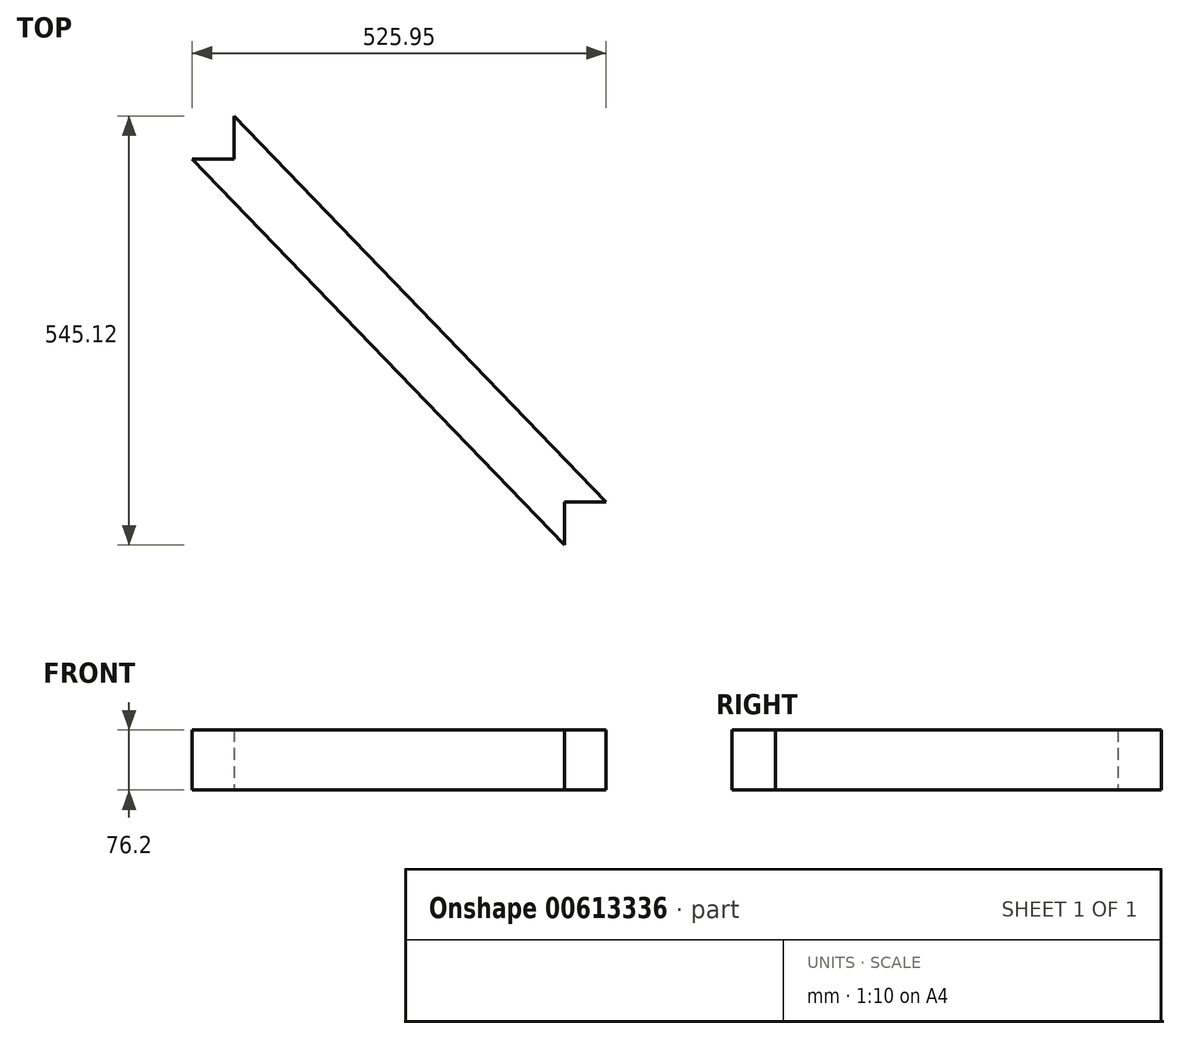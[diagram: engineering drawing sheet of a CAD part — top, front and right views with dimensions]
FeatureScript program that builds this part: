
annotation { "Feature Type Name" : "Feature", "Feature Type Description" : "" }
export const myFeature = defineFeature(function(context is Context, id is Id, definition is map)
    precondition{}
    {
        {
            var Q0;
            Q0=qCreatedBy(makeId("Top.planeOp"),FACE);
            var sketch = newSketch(context, id + "F0", { "sketchPlane" : qUnion([Q0])});
            skLineSegment(sketch, "E0.bottom", {"start": v(14.84, 38.1) * mm, "end": v(-38.1, 38.1) * mm});
            skLineSegment(sketch, "E0.right", {"start": v(-38.1, 38.1) * mm, "end": v(-38.1, -16.77) * mm});
            skPoint(sketch, "E0.middle", {"position": v(0, 0) * mm});
            skLineSegment(sketch, "E1.bottom", {"start": v(-458.17, 473.48) * mm, "end": v(-511.11, 473.48) * mm});
            skLineSegment(sketch, "E1.left", {"start": v(-458.17, 473.48) * mm, "end": v(-458.17, 528.35) * mm});
            skLineSegment(sketch, "E2.0", {"start": v(-511.11, 473.48) * mm, "end": v(-38.1, -16.77) * mm});
            skLineSegment(sketch, "E3.0", {"start": v(-458.17, 528.35) * mm, "end": v(14.84, 38.1) * mm});
            skPoint(sketch, "E0.left.start.orphan", {"position": v(38.1, 38.1) * mm});
            skPoint(sketch, "E0.top.start.orphan", {"position": v(38.1, -38.1) * mm});
            skPoint(sketch, "E4.orphan", {"position": v(-38.1, -38.1) * mm});
            skSolve(sketch);
        }
        {
            var Q0;
            Q0 = qSketchRegion(id + "F0", true);
            extrude(context, id + "F1", {"entities" : qUnion([Q0]), "depth" : 76.2 * mm, "offsetDistance" : 25.4 * mm});
        }
    });
